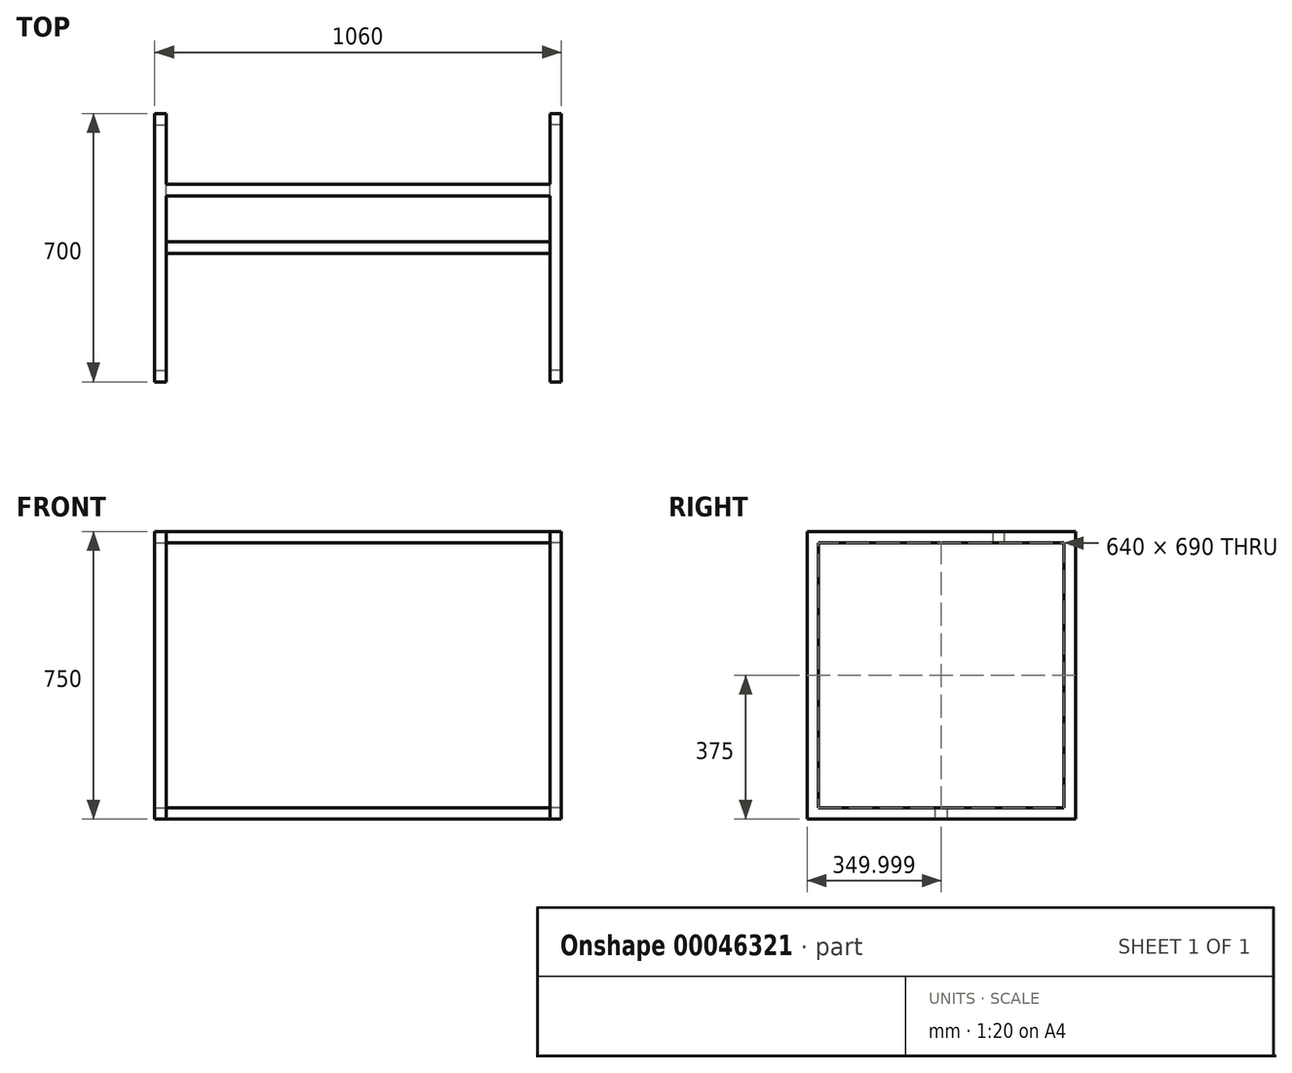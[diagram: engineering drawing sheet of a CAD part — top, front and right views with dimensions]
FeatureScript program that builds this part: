
annotation { "Feature Type Name" : "Feature", "Feature Type Description" : "" }
export const myFeature = defineFeature(function(context is Context, id is Id, definition is map)
    precondition{}
    {
        {
            var Q0;
            Q0=qCreatedBy(makeId("Right.planeOp"),FACE);
            var sketch = newSketch(context, id + "F0", { "sketchPlane" : qUnion([Q0])});
            skLineSegment(sketch, "E0", {"start": v(-493.15, 0) * mm, "end": v(-493.15, -750) * mm});
            skLineSegment(sketch, "E1", {"start": v(-493.15, -750) * mm, "end": v(206.85, -750) * mm});
            skLineSegment(sketch, "E2", {"start": v(206.85, -750) * mm, "end": v(206.85, 0) * mm});
            skLineSegment(sketch, "E3", {"start": v(206.85, 0) * mm, "end": v(-493.15, 0) * mm});
            skLineSegment(sketch, "E4.0", {"start": v(176.85, -30) * mm, "end": v(-463.15, -30) * mm});
            skLineSegment(sketch, "E4.1", {"start": v(176.85, -720) * mm, "end": v(176.85, -30) * mm});
            skLineSegment(sketch, "E4.2", {"start": v(-463.15, -720) * mm, "end": v(176.85, -720) * mm});
            skLineSegment(sketch, "E4.3", {"start": v(-463.15, -30) * mm, "end": v(-463.15, -720) * mm});
            skSolve(sketch);
        }
        {
            var Q0;
            Q0=makeQuery(id+"F0.imprint","IMPRINT",FACE,{"disambiguationData":[TD([[makeQuery(id+"F0.imprint","IMPRINT",EDGE,{"derivedFrom":sQuery(id+"F0.wireOp",EDGE,"E0")}),1.0]])]});
            extrude(context, id + "F1", {"entities" : qUnion([Q0]), "depth" : 30 * mm});
        }
        {
            var Q0;
            Q0=makeQuery(id+"F1.opExtrude","CAP_FACE",FACE,{"disambiguationData":[OSD([sQuery(id+"F0.wireOp",EDGE,"E0"),sQuery(id+"F0.wireOp",EDGE,"E1"),sQuery(id+"F0.wireOp",EDGE,"E2"),sQuery(id+"F0.wireOp",EDGE,"E3"),sQuery(id+"F0.wireOp",EDGE,"E4.0"),sQuery(id+"F0.wireOp",EDGE,"E4.1"),sQuery(id+"F0.wireOp",EDGE,"E4.2"),sQuery(id+"F0.wireOp",EDGE,"E4.3")])],"isStart":true});
            var sketch = newSketch(context, id + "F2", { "sketchPlane" : qUnion([Q0])});
            skLineSegment(sketch, "E5.rect.bottom", {"start": v(8.15, -30) * mm, "end": v(-21.85, -30) * mm});
            skLineSegment(sketch, "E5.rect.top", {"start": v(8.15, 0) * mm, "end": v(-21.85, 0) * mm});
            skLineSegment(sketch, "E5.rect.left", {"start": v(8.15, -30) * mm, "end": v(8.15, 0) * mm});
            skLineSegment(sketch, "E5.rect.right", {"start": v(-21.85, -30) * mm, "end": v(-21.85, 0) * mm});
            skPoint(sketch, "E5.rect.middle", {"position": v(-6.85, -15) * mm});
            skSolve(sketch);
        }
        {
            var Q0;
            Q0 = qSketchRegion(id + "F2", true);
            extrude(context, id + "F3", {"entities" : qUnion([Q0]), "operationType" : NewBodyOperationType.ADD, "depth" : 500 * mm});
        }
        {
            var Q0;
            Q0=makeQuery(id+"F1.opExtrude","SWEPT_BODY",BODY,{"disambiguationData":[OSD([sQuery(id+"F0.wireOp",EDGE,"E0"),sQuery(id+"F0.wireOp",EDGE,"E1"),sQuery(id+"F0.wireOp",EDGE,"E2"),sQuery(id+"F0.wireOp",EDGE,"E3"),sQuery(id+"F0.wireOp",EDGE,"E4.0"),sQuery(id+"F0.wireOp",EDGE,"E4.1"),sQuery(id+"F0.wireOp",EDGE,"E4.2"),sQuery(id+"F0.wireOp",EDGE,"E4.3")])]});
            var Q1;
            Q1=makeQuery(id+"F3.opExtrude","CAP_FACE",FACE,{"disambiguationData":[OSD([sQuery(id+"F2.wireOp",EDGE,"E5.rect.bottom"),sQuery(id+"F2.wireOp",EDGE,"E5.rect.top"),sQuery(id+"F2.wireOp",EDGE,"E5.rect.left"),sQuery(id+"F2.wireOp",EDGE,"E5.rect.right")])],"isStart":false});
            mirror(context, id + "F4", {"operationType" : NewBodyOperationType.ADD, "entities" : qUnion([Q0]), "mirrorPlane" : qUnion([Q1])});
        }
        {
            var Q0;
            Q0=makeQuery(id+"F1.opExtrude","CAP_FACE",FACE,{"disambiguationData":[OSD([sQuery(id+"F0.wireOp",EDGE,"E0"),sQuery(id+"F0.wireOp",EDGE,"E1"),sQuery(id+"F0.wireOp",EDGE,"E2"),sQuery(id+"F0.wireOp",EDGE,"E3"),sQuery(id+"F0.wireOp",EDGE,"E4.0"),sQuery(id+"F0.wireOp",EDGE,"E4.1"),sQuery(id+"F0.wireOp",EDGE,"E4.2"),sQuery(id+"F0.wireOp",EDGE,"E4.3")])],"isStart":true});
            var sketch = newSketch(context, id + "F5", { "sketchPlane" : qUnion([Q0])});
            skLineSegment(sketch, "E6", {"start": v(143.15, -750) * mm, "end": v(158.15, -750) * mm});
            skLineSegment(sketch, "E7", {"start": v(158.15, -750) * mm, "end": v(158.15, -720) * mm});
            skLineSegment(sketch, "E8", {"start": v(158.15, -720) * mm, "end": v(128.15, -720) * mm});
            skLineSegment(sketch, "E9", {"start": v(128.15, -720) * mm, "end": v(128.15, -750) * mm});
            skLineSegment(sketch, "E10", {"start": v(128.15, -750) * mm, "end": v(143.15, -750) * mm});
            skSolve(sketch);
        }
        {
            var Q0;
            Q0 = qSketchRegion(id + "F5", true);
            extrude(context, id + "F6", {"entities" : qUnion([Q0]), "operationType" : NewBodyOperationType.ADD, "endBound" : BoundingType.UP_TO_NEXT, "depth" : 25 * mm});
        }
    });
